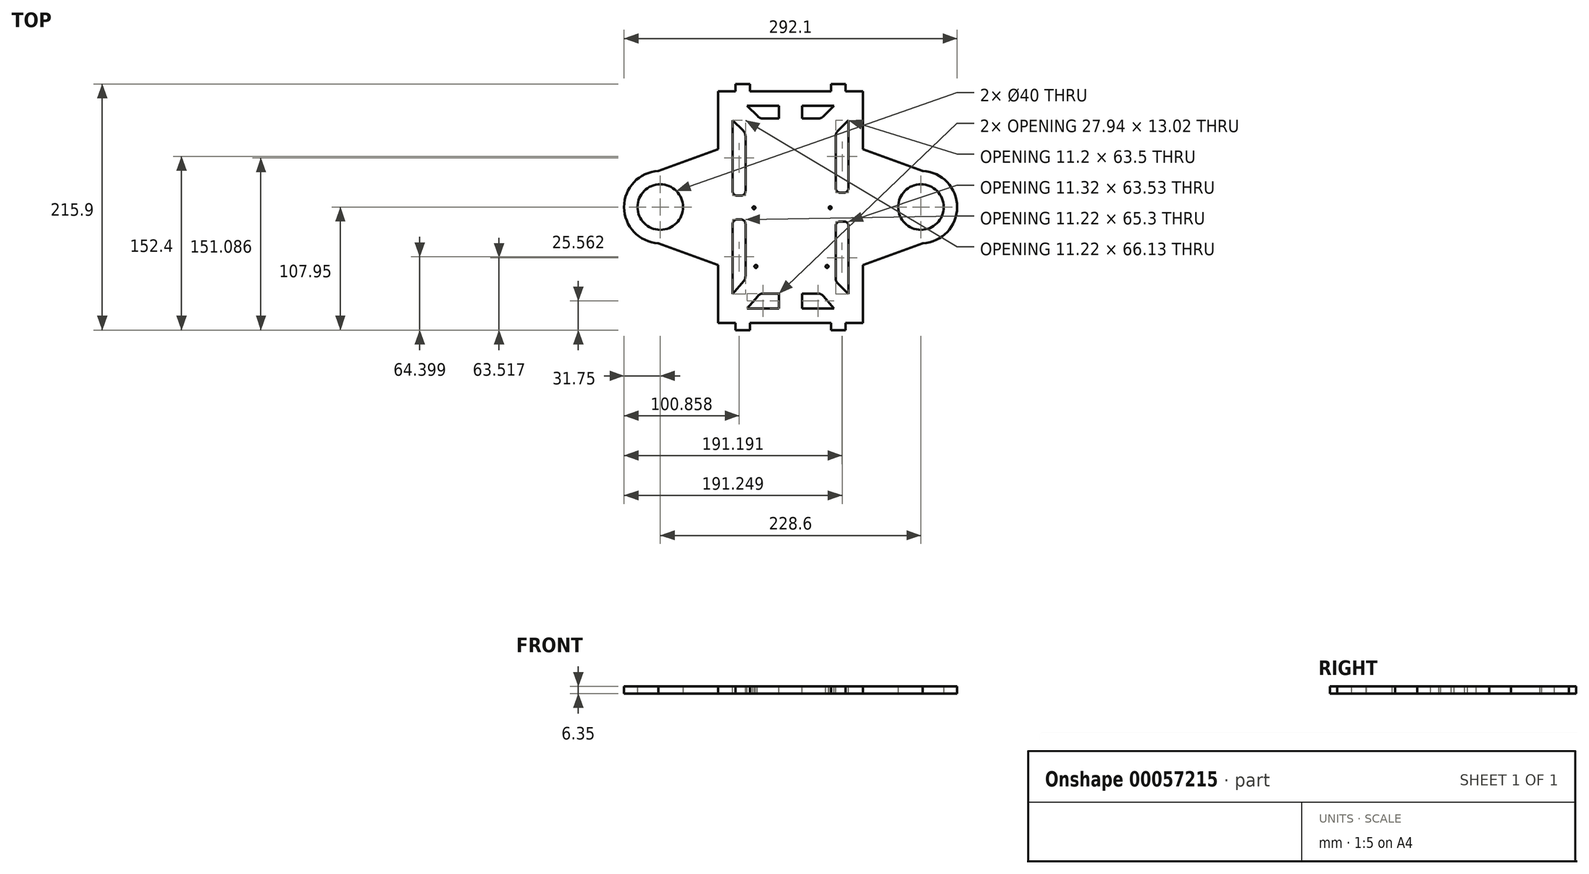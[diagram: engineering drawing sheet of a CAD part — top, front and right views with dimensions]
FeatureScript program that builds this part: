
annotation { "Feature Type Name" : "Feature", "Feature Type Description" : "" }
export const myFeature = defineFeature(function(context is Context, id is Id, definition is map)
    precondition{}
    {
        {
            var Q0;
            Q0=qCreatedBy(makeId("Top.planeOp"),FACE);
            var sketch = newSketch(context, id + "F0", { "sketchPlane" : qUnion([Q0])});
            skLineSegment(sketch, "E0.bottom", {"start": v(-63.5, 101.6) * mm, "end": v(63.5, 101.6) * mm});
            skLineSegment(sketch, "E0.top", {"start": v(-63.5, -101.6) * mm, "end": v(63.5, -101.6) * mm});
            skLineSegment(sketch, "E0.left", {"start": v(-63.5, 101.6) * mm, "end": v(-63.5, -101.6) * mm});
            skLineSegment(sketch, "E0.right", {"start": v(63.5, 101.6) * mm, "end": v(63.5, -101.6) * mm});
            skLineSegment(sketch, "E1.bottom", {"start": v(48.26, 101.6) * mm, "end": v(35.56, 101.6) * mm});
            skLineSegment(sketch, "E1.top", {"start": v(48.26, 107.95) * mm, "end": v(35.56, 107.95) * mm});
            skLineSegment(sketch, "E1.left", {"start": v(48.26, 101.6) * mm, "end": v(48.26, 107.95) * mm});
            skLineSegment(sketch, "E1.right", {"start": v(35.56, 101.6) * mm, "end": v(35.56, 107.95) * mm});
            skLineSegment(sketch, "E2.bottom", {"start": v(-48.26, 101.6) * mm, "end": v(-35.56, 101.6) * mm});
            skLineSegment(sketch, "E2.top", {"start": v(-48.26, 107.95) * mm, "end": v(-35.56, 107.95) * mm});
            skLineSegment(sketch, "E2.left", {"start": v(-48.26, 101.6) * mm, "end": v(-48.26, 107.95) * mm});
            skLineSegment(sketch, "E2.right", {"start": v(-35.56, 101.6) * mm, "end": v(-35.56, 107.95) * mm});
            skLineSegment(sketch, "E3.MirrorCS", {"start": v(-48.26, -107.95) * mm, "end": v(-35.56, -107.95) * mm});
            skLineSegment(sketch, "E4.MirrorCS", {"start": v(-48.26, -101.6) * mm, "end": v(-35.56, -101.6) * mm});
            skLineSegment(sketch, "E5.MirrorCS", {"start": v(-48.26, -101.6) * mm, "end": v(-48.26, -107.95) * mm});
            skLineSegment(sketch, "E6.MirrorCS", {"start": v(-35.56, -101.6) * mm, "end": v(-35.56, -107.95) * mm});
            skLineSegment(sketch, "E7.MirrorCS", {"start": v(35.56, -101.6) * mm, "end": v(35.56, -107.95) * mm});
            skLineSegment(sketch, "E8.MirrorCS", {"start": v(48.26, -107.95) * mm, "end": v(35.56, -107.95) * mm});
            skLineSegment(sketch, "E9.MirrorCS", {"start": v(48.26, -101.6) * mm, "end": v(48.26, -107.95) * mm});
            skLineSegment(sketch, "E10.MirrorCS", {"start": v(48.26, -101.6) * mm, "end": v(35.56, -101.6) * mm});
            skLineSegment(sketch, "E11", {"start": v(-63.5, 50.8) * mm, "end": v(-115.96, 31.7) * mm});
            skLineSegment(sketch, "E12", {"start": v(-63.5, -50.8) * mm, "end": v(-115.96, -31.7) * mm});
            skCircle(sketch, "E13", {"center": v(-114.3, 0) * mm, "radius": 31.75 * mm});
            skCircle(sketch, "E14", {"center": v(-114.3, 0) * mm, "radius": 20 * mm});
            skLineSegment(sketch, "E15.MirrorCS", {"start": v(63.5, 50.8) * mm, "end": v(115.96, 31.7) * mm});
            skLineSegment(sketch, "E16.MirrorCS", {"start": v(63.5, -50.8) * mm, "end": v(115.96, -31.7) * mm});
            skCircle(sketch, "E17.MirrorC", {"center": v(114.3, 0) * mm, "radius": 31.75 * mm});
            skCircle(sketch, "E18.MirrorC", {"center": v(114.3, 0) * mm, "radius": 20 * mm});
            skSolve(sketch);
        }
        {
            var Q0;
            Q0=qSketchRegion(id+"F0",true);
            extrude(context, id + "F1", {"entities" : qUnion([Q0]), "depth" : 6.35 * mm});
        }
        {
            var Q0;
            Q0=makeQuery(id+"F1.opExtrude","CAP_FACE",FACE,{"disambiguationData":[OSD([sQuery(id+"F0.wireOp",EDGE,"E0.bottom"),sQuery(id+"F0.wireOp",EDGE,"E0.top"),sQuery(id+"F0.wireOp",EDGE,"E0.left"),sQuery(id+"F0.wireOp",EDGE,"E0.right"),sQuery(id+"F0.wireOp",EDGE,"E1.top"),sQuery(id+"F0.wireOp",EDGE,"E1.left"),sQuery(id+"F0.wireOp",EDGE,"E1.right"),sQuery(id+"F0.wireOp",EDGE,"E2.top"),sQuery(id+"F0.wireOp",EDGE,"E2.left"),sQuery(id+"F0.wireOp",EDGE,"E2.right"),sQuery(id+"F0.wireOp",EDGE,"E3.MirrorCS"),sQuery(id+"F0.wireOp",EDGE,"E5.MirrorCS"),sQuery(id+"F0.wireOp",EDGE,"E6.MirrorCS"),sQuery(id+"F0.wireOp",EDGE,"E7.MirrorCS"),sQuery(id+"F0.wireOp",EDGE,"E8.MirrorCS"),sQuery(id+"F0.wireOp",EDGE,"E9.MirrorCS"),sQuery(id+"F0.wireOp",EDGE,"E11"),sQuery(id+"F0.wireOp",EDGE,"E12"),sQuery(id+"F0.wireOp",EDGE,"E13"),sQuery(id+"F0.wireOp",EDGE,"E14"),sQuery(id+"F0.wireOp",EDGE,"E15.MirrorCS"),sQuery(id+"F0.wireOp",EDGE,"E16.MirrorCS"),sQuery(id+"F0.wireOp",EDGE,"E17.MirrorC"),sQuery(id+"F0.wireOp",EDGE,"E18.MirrorC")])],"isStart":false});
            var sketch = newSketch(context, id + "F2", { "sketchPlane" : qUnion([Q0])});
            skLineSegment(sketch, "E19.bottom", {"start": v(-24.25, 77.67) * mm, "end": v(24.25, 77.67) * mm});
            skLineSegment(sketch, "E19.top", {"start": v(-23.97, -75.88) * mm, "end": v(23.98, -75.88) * mm});
            skLineSegment(sketch, "E19.left", {"start": v(-39.58, 62.34) * mm, "end": v(-39.58, 13.88) * mm});
            skLineSegment(sketch, "E19.right", {"start": v(39.6, 62.35) * mm, "end": v(39.6, 16.5) * mm});
            skPoint(sketch, "E20.visualSharp", {"position": v(-39.58, 77.67) * mm});
            skPoint(sketch, "E21.visualSharp", {"position": v(39.6, 77.67) * mm});
            skPoint(sketch, "E22.visualSharp", {"position": v(39.6, -75.88) * mm});
            skArc(sketch, "E22.filletArc", {"start": v(26.9, -75.88) * mm, "mid": v(35.23, -72.76) * mm, "end": v(39.48, -64.93) * mm});
            skPoint(sketch, "E23.visualSharp", {"position": v(-39.58, -75.88) * mm});
            skArc(sketch, "E24.filletArc", {"start": v(-38.1, 88.9) * mm, "mid": v(-47.08, 85.18) * mm, "end": v(-50.8, 76.2) * mm});
            skLineSegment(sketch, "E25.left", {"start": v(-50.8, -14.71) * mm, "end": v(-50.8, -76.2) * mm});
            skArc(sketch, "E26.filletArc", {"start": v(-50.8, -76.2) * mm, "mid": v(-47.08, -85.18) * mm, "end": v(-38.1, -88.9) * mm});
            skLineSegment(sketch, "E25.top", {"start": v(-38.1, -88.9) * mm, "end": v(38.1, -88.9) * mm});
            skArc(sketch, "E27.filletArc", {"start": v(38.1, -88.9) * mm, "mid": v(47.08, -85.18) * mm, "end": v(50.8, -76.2) * mm});
            skLineSegment(sketch, "E25.right", {"start": v(50.8, -16.48) * mm, "end": v(50.8, -76.2) * mm});
            skArc(sketch, "E28.filletArc", {"start": v(50.8, 76.2) * mm, "mid": v(47.08, 85.18) * mm, "end": v(38.1, 88.9) * mm});
            skLineSegment(sketch, "E25.bottom", {"start": v(-38.1, 88.9) * mm, "end": v(38.1, 88.9) * mm});
            skLineSegment(sketch, "E29", {"start": v(-46.99, 10.07) * mm, "end": v(-43.4, 10.07) * mm});
            skLineSegment(sketch, "E30", {"start": v(-43.4, -10.9) * mm, "end": v(-46.99, -10.9) * mm});
            skLineSegment(sketch, "E31", {"start": v(43.4, 12.7) * mm, "end": v(47, 12.7) * mm});
            skLineSegment(sketch, "E32", {"start": v(43.4, -12.67) * mm, "end": v(47, -12.67) * mm});
            skLineSegment(sketch, "E33", {"start": v(10.16, -75.88) * mm, "end": v(10.16, -88.9) * mm});
            skLineSegment(sketch, "E34", {"start": v(-10.16, -75.88) * mm, "end": v(-10.16, -88.9) * mm});
            skLineSegment(sketch, "E35", {"start": v(-10.16, 77.67) * mm, "end": v(-10.16, 88.9) * mm});
            skLineSegment(sketch, "E36", {"start": v(10.16, 77.67) * mm, "end": v(10.16, 88.9) * mm});
            skLineSegment(sketch, "E37", {"start": v(-41.12, -64.96) * mm, "end": v(-50.8, -76.2) * mm});
            skLineSegment(sketch, "E38", {"start": v(-28.78, -78.08) * mm, "end": v(-38.1, -88.9) * mm});
            skLineSegment(sketch, "E39", {"start": v(28.8, -78.08) * mm, "end": v(38.1, -88.9) * mm});
            skLineSegment(sketch, "E40", {"start": v(41.35, -66.8) * mm, "end": v(50.8, -76.2) * mm});
            skLineSegment(sketch, "E41", {"start": v(41.45, 66.83) * mm, "end": v(50.8, 76.2) * mm});
            skLineSegment(sketch, "E42", {"start": v(38.1, 88.9) * mm, "end": v(28.74, 79.54) * mm});
            skLineSegment(sketch, "E43", {"start": v(-28.74, 79.54) * mm, "end": v(-38.1, 88.9) * mm});
            skLineSegment(sketch, "E44", {"start": v(-41.44, 66.83) * mm, "end": v(-50.8, 76.2) * mm});
            skArc(sketch, "E45.filletArc", {"start": v(-43.4, 10.07) * mm, "mid": v(-40.7, 11.19) * mm, "end": v(-39.58, 13.88) * mm});
            skLineSegment(sketch, "E46", {"start": v(-39.58, -60.82) * mm, "end": v(-39.58, -14.71) * mm});
            skArc(sketch, "E47.filletArc", {"start": v(39.6, 16.5) * mm, "mid": v(40.71, 13.82) * mm, "end": v(43.4, 12.7) * mm});
            skPoint(sketch, "E48.visualSharp", {"position": v(-39.58, -10.9) * mm});
            skArc(sketch, "E48.filletArc", {"start": v(-39.58, -14.71) * mm, "mid": v(-40.7, -12.02) * mm, "end": v(-43.4, -10.9) * mm});
            skPoint(sketch, "E49.visualSharp", {"position": v(-39.58, 64.97) * mm});
            skArc(sketch, "E49.filletArc", {"start": v(-39.58, 62.34) * mm, "mid": v(-40.07, 64.77) * mm, "end": v(-41.44, 66.83) * mm});
            skPoint(sketch, "E50.visualSharp", {"position": v(-26.88, 77.67) * mm});
            skArc(sketch, "E50.filletArc", {"start": v(-28.74, 79.54) * mm, "mid": v(-26.68, 78.16) * mm, "end": v(-24.25, 77.67) * mm});
            skLineSegment(sketch, "E51", {"start": v(39.48, -62.28) * mm, "end": v(39.59, -16.47) * mm});
            skPoint(sketch, "E52.visualSharp", {"position": v(39.6, -12.67) * mm});
            skArc(sketch, "E52.filletArc", {"start": v(43.4, -12.67) * mm, "mid": v(40.7, -13.78) * mm, "end": v(39.59, -16.47) * mm});
            skPoint(sketch, "E53.visualSharp", {"position": v(39.6, 64.97) * mm});
            skArc(sketch, "E53.filletArc", {"start": v(41.45, 66.83) * mm, "mid": v(40.08, 64.77) * mm, "end": v(39.6, 62.35) * mm});
            skPoint(sketch, "E54.visualSharp", {"position": v(26.88, 77.67) * mm});
            skArc(sketch, "E54.filletArc", {"start": v(24.25, 77.67) * mm, "mid": v(26.68, 78.16) * mm, "end": v(28.74, 79.54) * mm});
            skPoint(sketch, "E55.visualSharp", {"position": v(-39.58, -63.18) * mm});
            skArc(sketch, "E55.filletArc", {"start": v(-41.12, -64.96) * mm, "mid": v(-39.98, -63.03) * mm, "end": v(-39.58, -60.82) * mm});
            skPoint(sketch, "E56.visualSharp", {"position": v(-26.88, -75.88) * mm});
            skArc(sketch, "E56.filletArc", {"start": v(-23.97, -75.88) * mm, "mid": v(-26.62, -76.45) * mm, "end": v(-28.78, -78.08) * mm});
            skPoint(sketch, "E57.visualSharp", {"position": v(26.9, -75.88) * mm});
            skArc(sketch, "E57.filletArc", {"start": v(28.8, -78.08) * mm, "mid": v(26.63, -76.45) * mm, "end": v(23.98, -75.88) * mm});
            skPoint(sketch, "E58.visualSharp", {"position": v(39.48, -64.93) * mm});
            skArc(sketch, "E58.filletArc", {"start": v(39.48, -62.28) * mm, "mid": v(39.97, -64.73) * mm, "end": v(41.35, -66.8) * mm});
            skArc(sketch, "E59.filletArc", {"start": v(50.8, -16.48) * mm, "mid": v(49.68, -13.78) * mm, "end": v(47, -12.67) * mm});
            skLineSegment(sketch, "E60", {"start": v(50.8, 76.2) * mm, "end": v(50.8, 16.5) * mm});
            skPoint(sketch, "E61.visualSharp", {"position": v(50.8, 12.7) * mm});
            skArc(sketch, "E61.filletArc", {"start": v(47, 12.7) * mm, "mid": v(49.68, 13.82) * mm, "end": v(50.8, 16.5) * mm});
            skArc(sketch, "E62.filletArc", {"start": v(-46.99, -10.9) * mm, "mid": v(-49.68, -12.02) * mm, "end": v(-50.8, -14.71) * mm});
            skLineSegment(sketch, "E63", {"start": v(-50.8, 76.2) * mm, "end": v(-50.8, 13.88) * mm});
            skPoint(sketch, "E64.visualSharp", {"position": v(-50.8, 10.07) * mm});
            skArc(sketch, "E64.filletArc", {"start": v(-50.8, 13.88) * mm, "mid": v(-49.68, 11.19) * mm, "end": v(-46.99, 10.07) * mm});
            skSolve(sketch);
        }
        {
            var Q0;
            {var subQ1=sQuery(id+"F2.wireOp",EDGE,"E35");Q0=makeQuery(id+"F2.imprint","IMPRINT",FACE,{"disambiguationData":[TD([[makeQuery(id+"F2.imprint","IMPRINT",EDGE,{"derivedFrom":subQ1}),1.0]])]});}
            var Q1;
            {var subQ3=sQuery(id+"F2.wireOp",EDGE,"E34");Q1=makeQuery(id+"F2.imprint","IMPRINT",FACE,{"disambiguationData":[TD([[makeQuery(id+"F2.imprint","IMPRINT",EDGE,{"derivedFrom":subQ3}),-1.0]])]});}
            var Q2;
            {var subQ1=sQuery(id+"F2.wireOp",EDGE,"E33");Q2=makeQuery(id+"F2.imprint","IMPRINT",FACE,{"disambiguationData":[TD([[makeQuery(id+"F2.imprint","IMPRINT",EDGE,{"derivedFrom":subQ1}),1.0]])]});}
            var Q3;
            Q3=makeQuery(id+"F2.imprint","IMPRINT",FACE,{"disambiguationData":[TD([[makeQuery(id+"F2.imprint","IMPRINT",EDGE,{"derivedFrom":sQuery(id+"F2.wireOp",EDGE,"E25.right")}),-1.0]])]});
            var Q4;
            Q4=makeQuery(id+"F2.imprint","IMPRINT",FACE,{"disambiguationData":[TD([[makeQuery(id+"F2.imprint","IMPRINT",EDGE,{"derivedFrom":sQuery(id+"F2.wireOp",EDGE,"E25.left")}),1.0]])]});
            var Q5;
            Q5=makeQuery(id+"F2.imprint","IMPRINT",FACE,{"disambiguationData":[TD([[makeQuery(id+"F2.imprint","IMPRINT",EDGE,{"derivedFrom":sQuery(id+"F2.wireOp",EDGE,"E19.right")}),1.0]])]});
            var Q6;
            {var subQ1=sQuery(id+"F2.wireOp",EDGE,"E36");Q6=makeQuery(id+"F2.imprint","IMPRINT",FACE,{"disambiguationData":[TD([[makeQuery(id+"F2.imprint","IMPRINT",EDGE,{"derivedFrom":subQ1}),-1.0]])]});}
            var Q7;
            Q7=makeQuery(id+"F2.imprint","IMPRINT",FACE,{"disambiguationData":[TD([[makeQuery(id+"F2.imprint","IMPRINT",EDGE,{"derivedFrom":sQuery(id+"F2.wireOp",EDGE,"E19.left")}),-1.0]])]});
            extrude(context, id + "F3", {"entities" : qUnion([Q0, Q1, Q2, Q3, Q4, Q5, Q6, Q7]), "operationType" : NewBodyOperationType.REMOVE, "oppositeDirection" : true, "depth" : 25.4 * mm});
        }
        {
            var Q0;
            Q0=makeQuery(id+"F1.opExtrude","CAP_FACE",FACE,{"disambiguationData":[OSD([sQuery(id+"F0.wireOp",EDGE,"E0.bottom"),sQuery(id+"F0.wireOp",EDGE,"E0.top"),sQuery(id+"F0.wireOp",EDGE,"E0.left"),sQuery(id+"F0.wireOp",EDGE,"E0.right"),sQuery(id+"F0.wireOp",EDGE,"E1.top"),sQuery(id+"F0.wireOp",EDGE,"E1.left"),sQuery(id+"F0.wireOp",EDGE,"E1.right"),sQuery(id+"F0.wireOp",EDGE,"E2.top"),sQuery(id+"F0.wireOp",EDGE,"E2.left"),sQuery(id+"F0.wireOp",EDGE,"E2.right"),sQuery(id+"F0.wireOp",EDGE,"E3.MirrorCS"),sQuery(id+"F0.wireOp",EDGE,"E5.MirrorCS"),sQuery(id+"F0.wireOp",EDGE,"E6.MirrorCS"),sQuery(id+"F0.wireOp",EDGE,"E7.MirrorCS"),sQuery(id+"F0.wireOp",EDGE,"E8.MirrorCS"),sQuery(id+"F0.wireOp",EDGE,"E9.MirrorCS"),sQuery(id+"F0.wireOp",EDGE,"E11"),sQuery(id+"F0.wireOp",EDGE,"E12"),sQuery(id+"F0.wireOp",EDGE,"E13"),sQuery(id+"F0.wireOp",EDGE,"E14"),sQuery(id+"F0.wireOp",EDGE,"E15.MirrorCS"),sQuery(id+"F0.wireOp",EDGE,"E16.MirrorCS"),sQuery(id+"F0.wireOp",EDGE,"E17.MirrorC"),sQuery(id+"F0.wireOp",EDGE,"E18.MirrorC")])],"isStart":false});
            var sketch = newSketch(context, id + "F4", { "sketchPlane" : qUnion([Q0])});
            skCircle(sketch, "E65", {"center": v(31.96, -52.06) * mm, "radius": 1.27 * mm});
            skCircle(sketch, "E66", {"center": v(-30.42, -52.06) * mm, "radius": 1.27 * mm});
            skLineSegment(sketch, "E67", {"start": v(-31.55, -52.06) * mm, "end": v(32.12, -52.06) * mm});
            skLineSegment(sketch, "E68", {"start": v(-48.36, -0.58) * mm, "end": v(60.42, -0.58) * mm});
            skCircle(sketch, "E69", {"center": v(-32.12, -0.58) * mm, "radius": 1.27 * mm});
            skCircle(sketch, "E70", {"center": v(34.7, -0.58) * mm, "radius": 1.27 * mm});
            skSolve(sketch);
        }
        {
            var Q0;
            Q0=qSketchRegion(id+"F4",true);
            extrude(context, id + "F5", {"entities" : qUnion([Q0]), "operationType" : NewBodyOperationType.REMOVE, "oppositeDirection" : true, "depth" : 25.4 * mm});
        }
    });
